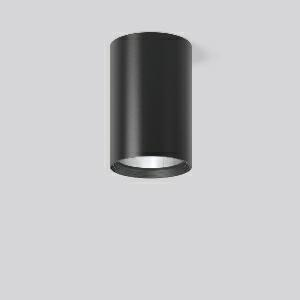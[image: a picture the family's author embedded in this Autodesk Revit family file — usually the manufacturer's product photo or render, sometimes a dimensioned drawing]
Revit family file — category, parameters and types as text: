
# Revit family: heledon_maxi_a_931218_003_76_b4c4
name_source: partatom
category: Lighting Fixtures
units: mm (PartAtom-declared; Revit-internal decimal feet)

## family parameters
Cut with Voids When Loaded = No
Host = Face
Light Source = No
Part Type = Normal
Room Calculation Point = No
Round Connector Dimension = Use Diameter
Shared = No

## types (1)
- HELEDON maxi A (1 x LED Modul 930, 3350 lm, 3000)
    Apparent Load = 25 VA
    Approval mark = CE
    CIE Flux Codes = 100 100 100 100 100
    Color Rendering = 90
    Color Temperature = 3000
    Default Elevation = 1800 mm
    Description = Series: HELEDON maxi
Cylindrical surface-mounted downlight. Housing: die-cast aluminium, powder-coated. Internal ceiling frame polycarbonate with bayonet mounting. Black plastic ring and recessed LED to prevent glare from the side. Optical assembly with reflector made of MIRO-Silver with 98% total light reflection for outstanding efficiency - can be changed without tools. Best colour rendering index Ra>90. Suitable for Ceiling mounting. Easy installation with a separate ceiling frame with bayonet mounting and plug connection. Driver integrated. Connected via plug-in connector. High quality converter without flickering and stroboscopic effect. The following accessories can be mounted without use of tools: interchangeable lenses, decorative glasses, honeycomb louvre, clear and frosted diffusers, white interchangeable plastic ring. 
Colour: deep black, matt (RAL 9005)
Diameter: 123 mm
Height: 183 mm
Lamp: LED
Socket: without socket
Colour temperature: 3000K
Colour rendering index (CRI): 92
System power: 25 W
Rated luminous flux: 3350 lm
Luminous efficiency: 134 lm/W
Control gear: Converter, dimmable, DALI
Protection class: I
Type of protection: IP 20
    Height = 183 mm
    Lamp = 1 x LED Modul 930
    Lamp Light Flux = 3350 lm
    Lamp count = 1
    Length = 123 mm
    Lifetime = 50000 h
    Luminous efficacy = 134 lm/W
    Manufacturer = RZB
    ModVariant = No
    Model = 931218.003.76
    Mounting Place = Ceiling
    Mounting Type = Surface mounted
    Number of Poles = 1
    OnlyDefault = Yes
    Power Factor = 1
    Product Name = HELEDON maxi A
    Product group = Surface mounted downlights
    ProductGroupID = 302
    Protection Class = Protection class I
    Protection Degree = IP 20
    RLX_Detail_Level = 1
    RLX_Emergency_Light_Flux = 0 lm
    RLX_Emergency_Type = 0
    RLX_Emergency_Type_DB = No
    RlxData = <blob elided: 98929 chars, md5=8a197f02>
    Socket = socket
    Standby Power = 0 W
    System Light Flux = 3350 lm
    System Power = 25 W
    Type Comments = Product without accessories
    Type Image = 931192.003.jpg
    URL = http://relux.com
    VarID = ---
    Voltage = 230 V
    Voltage Range = 220-240 V
    Weight = 0.00 kg
    Width = 0 mm  [stored 0 ft]

note: [stored X ft] marks values corroborated as IEEE doubles in the binary element streams (Revit-internal decimal feet)

## geometry (parser evidence)
native form markers: Blend x4, Sweep x10
no freeform markers — native parametric forms only
